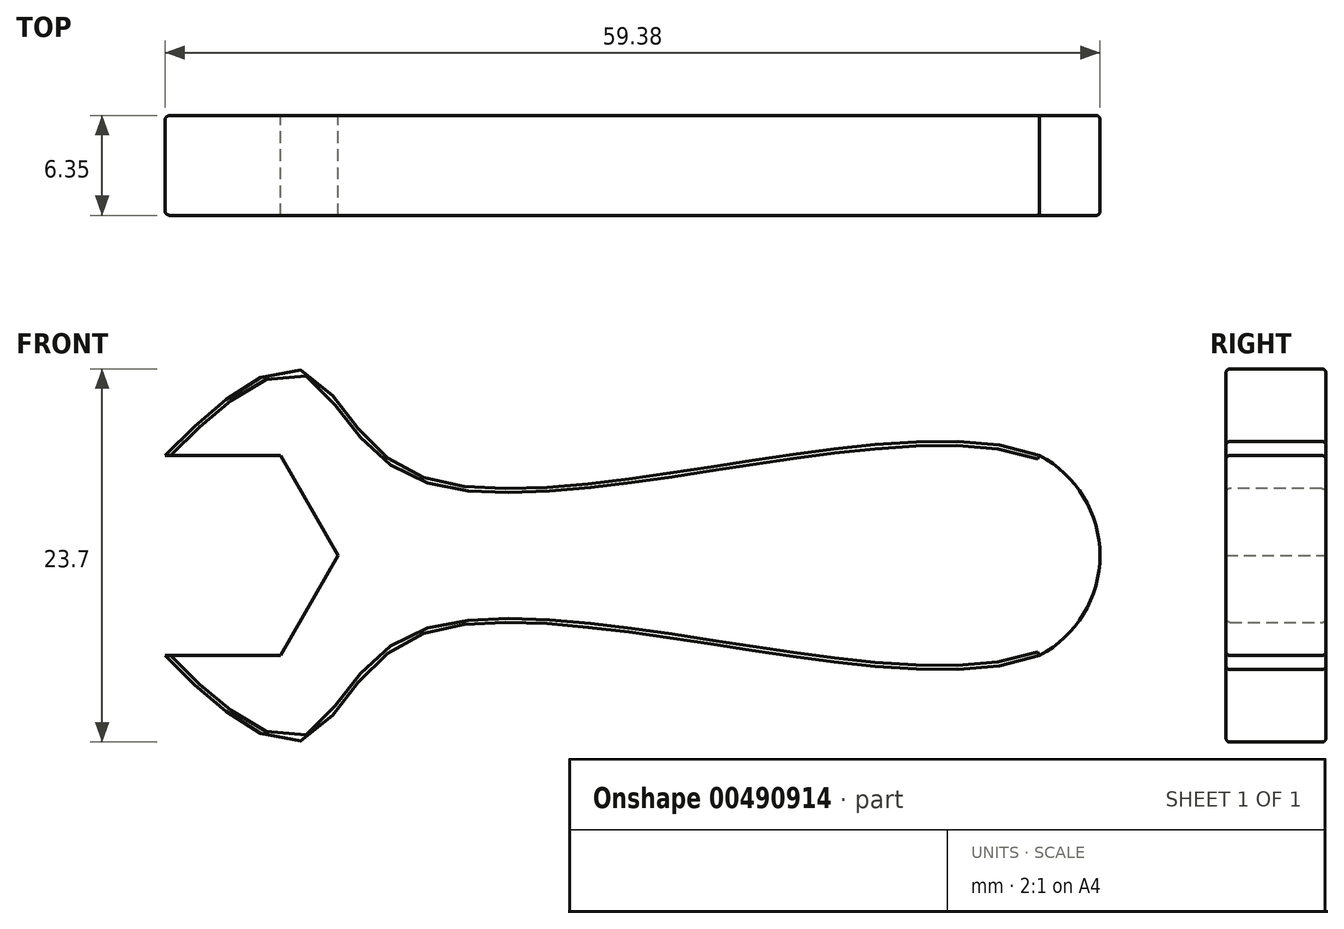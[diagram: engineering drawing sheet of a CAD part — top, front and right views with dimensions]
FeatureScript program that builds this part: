
annotation { "Feature Type Name" : "Feature", "Feature Type Description" : "" }
export const myFeature = defineFeature(function(context is Context, id is Id, definition is map)
    precondition{}
    {
        {
            var Q0;
            Q0=qCreatedBy(makeId("Front.planeOp"),FACE);
            var sketch = newSketch(context, id + "F0", { "sketchPlane" : qUnion([Q0])});
            skCircle(sketch, "E0.cCircle", {"center": v(0, 0) * mm, "radius": 6.35 * mm, "construction": true});
            skLineSegment(sketch, "E0.0", {"start": v(-3.67, 6.35) * mm, "end": v(3.67, 6.35) * mm});
            skLineSegment(sketch, "E0.1", {"start": v(3.67, 6.35) * mm, "end": v(7.33, 0) * mm});
            skLineSegment(sketch, "E0.2", {"start": v(7.33, 0) * mm, "end": v(3.67, -6.35) * mm});
            skLineSegment(sketch, "E0.3", {"start": v(3.67, -6.35) * mm, "end": v(-3.67, -6.35) * mm});
            skLineSegment(sketch, "E0.4", {"start": v(-3.67, -6.35) * mm, "end": v(-7.33, 0) * mm});
            skLineSegment(sketch, "E0.5", {"start": v(-7.33, 0) * mm, "end": v(-3.67, 6.35) * mm});
            skPoint(sketch, "E0.0.midPoint", {"position": v(0, 6.35) * mm});
            skFitSpline(sketch, "E1", {"points": [v(-3.67, -6.35) * mm, v(4.74, -11.83) * mm, v(12.46, -5.07) * mm, v(51.87, -6.35) * mm], "startDerivative": vector(22.68, -24.33) * mm, "endDerivative": vector(54.96, 21.15) * mm});
            skFitSpline(sketch, "E2.MirrorCS", {"points": [v(-3.67, 6.35) * mm, v(4.74, 11.83) * mm, v(12.46, 5.07) * mm, v(51.87, 6.35) * mm], "startDerivative": vector(22.68, 24.33) * mm, "endDerivative": vector(54.96, -21.15) * mm});
            skArc(sketch, "E3", {"start": v(51.87, -6.35) * mm, "mid": v(55.7, 0) * mm, "end": v(51.87, 6.35) * mm});
            skSolve(sketch);
        }
        {
            var Q0;
            Q0=makeQuery(id+"F0.imprint","IMPRINT",FACE,{"disambiguationData":[TD([[makeQuery(id+"F0.imprint","IMPRINT",EDGE,{"derivedFrom":sQuery(id+"F0.wireOp",EDGE,"E0.0")}),1.0]])]});
            extrude(context, id + "F1", {"entities" : qUnion([Q0]), "depth" : 6.35 * mm});
        }
        {
            var Q0;
            Q0=makeQuery(id+"F1.opExtrude","CAP_EDGE",EDGE,{"disambiguationData":[OSD([sQuery(id+"F0.wireOp",EDGE,"E2.MirrorCS")])],"isStart":false});
            var Q1;
            Q1=makeQuery(id+"F1.opExtrude","CAP_EDGE",EDGE,{"disambiguationData":[OSD([sQuery(id+"F0.wireOp",EDGE,"E3")])],"isStart":false});
            var Q2;
            Q2=makeQuery(id+"F1.opExtrude","CAP_EDGE",EDGE,{"disambiguationData":[OSD([sQuery(id+"F0.wireOp",EDGE,"E1")])],"isStart":false});
            var Q3;
            Q3=makeQuery(id+"F1.opExtrude","CAP_EDGE",EDGE,{"disambiguationData":[OSD([sQuery(id+"F0.wireOp",EDGE,"E2.MirrorCS")])],"isStart":true});
            var Q4;
            Q4=makeQuery(id+"F1.opExtrude","CAP_EDGE",EDGE,{"disambiguationData":[OSD([sQuery(id+"F0.wireOp",EDGE,"E3")])],"isStart":true});
            var Q5;
            Q5=makeQuery(id+"F1.opExtrude","CAP_EDGE",EDGE,{"disambiguationData":[OSD([sQuery(id+"F0.wireOp",EDGE,"E1")])],"isStart":true});
            fillet(context, id + "F2", {"entities" : qUnion([Q0, Q1, Q2, Q3, Q4, Q5]), "radius" : 0.25 * mm, "tangentPropagation" : true, "allowEdgeOverflow" : false});
        }
    });
